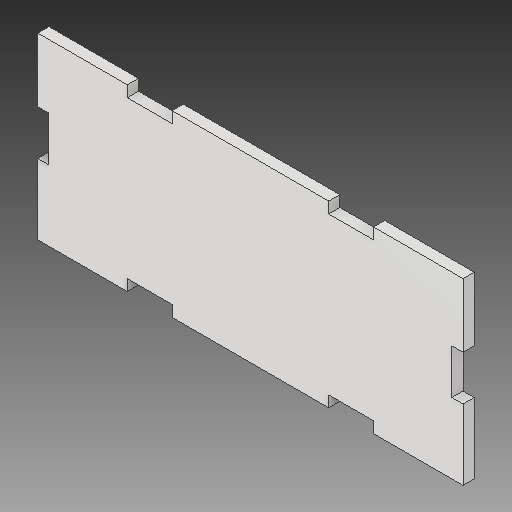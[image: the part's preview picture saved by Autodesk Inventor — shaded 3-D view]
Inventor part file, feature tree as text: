
AUTODESK INVENTOR PART (.ipt)
format: ipt  version: 2018.2 (Build 222227000, 227)  size: 124,416 bytes
history: native  units: in
note: dims shown in document units (in); Inventor stores cm internally (conversion verified against a paired STEP export)
features: reference x10, other x4, extrude x1, sketch x1
ambient origin geometry x8: Origin, YZ Plane, XZ Plane, XY Plane, X Axis, Y Axis, Z Axis, Center Point
bodies: Solid1 (feature_tree)
feature tree (16):
  extrude  "Extrusion1"  Depth=0.125in TaperAngle=0.0deg
  sketch  "Sketch1"  dims[d0=0.125in d1=0.125in d2=0.0in]
  reference  "Reference1"
  reference  "Reference2"
  reference  "Reference3"
  reference  "Reference4"
  reference  "Reference5"
  reference  "Reference6"
  reference  "Reference7"
  reference  "Reference8"
  reference  "Reference9"
  reference  "Reference10"
  other  "Assembly1.iam"
  other  "Side 2:1"
  other  "side:1"
  other  "Face:1"
